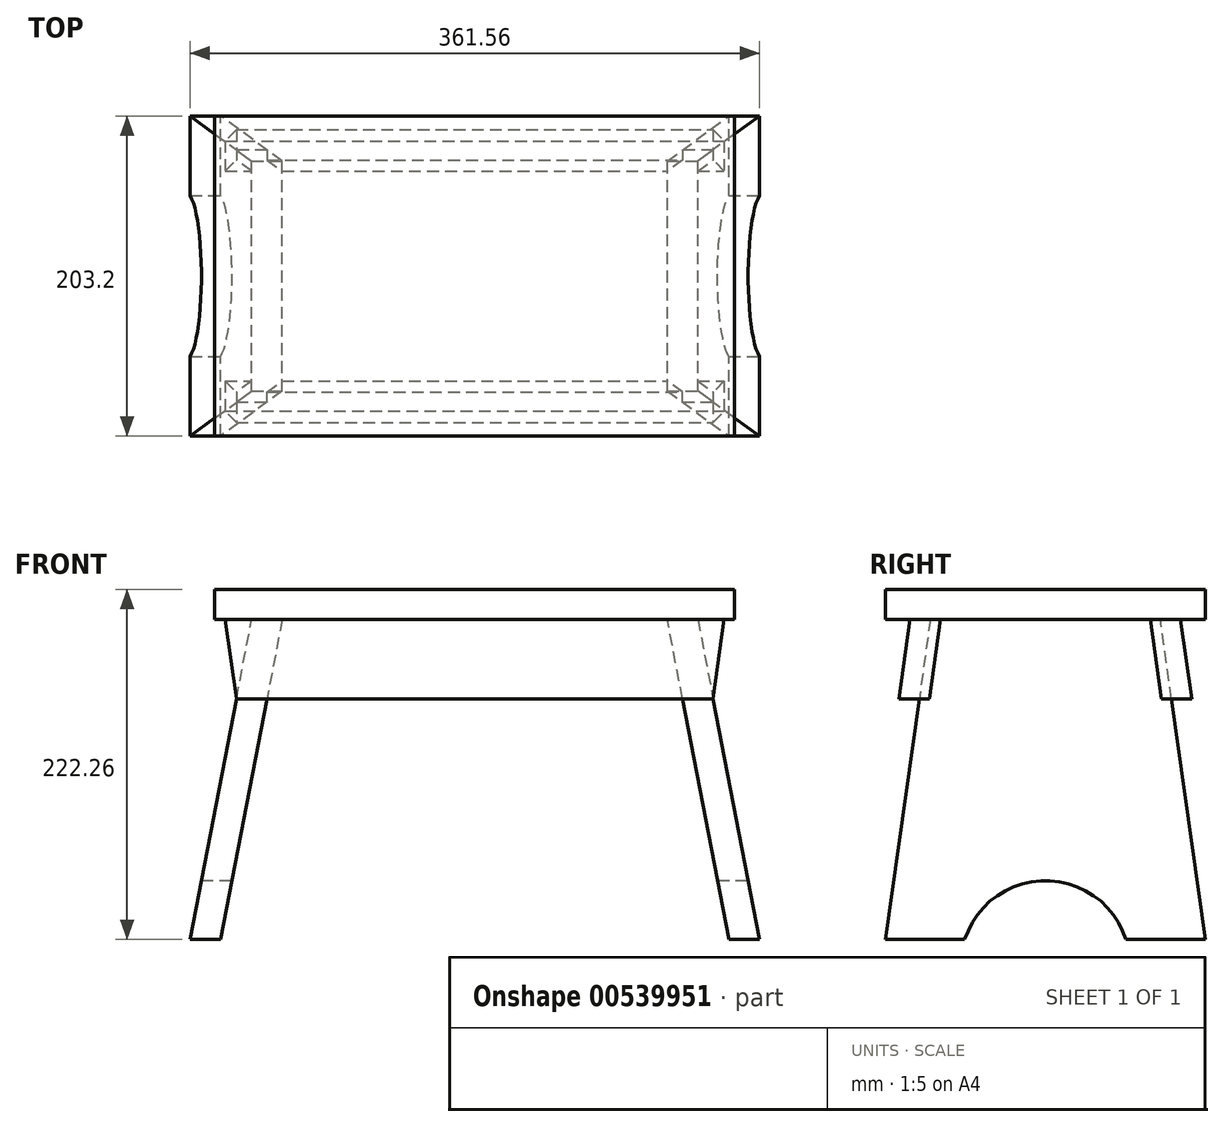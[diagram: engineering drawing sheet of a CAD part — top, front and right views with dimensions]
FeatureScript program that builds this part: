
annotation { "Feature Type Name" : "Feature", "Feature Type Description" : "" }
export const myFeature = defineFeature(function(context is Context, id is Id, definition is map)
    precondition{}
    {
        {
            var Q0;
            Q0=qCreatedBy(makeId("Front.planeOp"),FACE);
            var sketch = newSketch(context, id + "F0", { "sketchPlane" : qUnion([Q0])});
            skLineSegment(sketch, "E0.bottom", {"start": v(-165.1, 9.52) * mm, "end": v(165.1, 9.53) * mm});
            skLineSegment(sketch, "E0.top", {"start": v(-165.1, -9.53) * mm, "end": v(165.1, -9.52) * mm});
            skLineSegment(sketch, "E0.left", {"start": v(-165.1, 9.52) * mm, "end": v(-165.1, -9.53) * mm});
            skLineSegment(sketch, "E0.right", {"start": v(165.1, 9.52) * mm, "end": v(165.1, -9.53) * mm});
            skPoint(sketch, "E0.middle", {"position": v(0, 0) * mm});
            skLineSegment(sketch, "E1.bottom", {"start": v(-165.1, -9.53) * mm, "end": v(165.1, -9.52) * mm, "construction": true});
            skLineSegment(sketch, "E2", {"start": v(141.68, -9.53) * mm, "end": v(180.78, -212.73) * mm});
            skLineSegment(sketch, "E3", {"start": v(180.78, -212.73) * mm, "end": v(161.38, -212.73) * mm});
            skLineSegment(sketch, "E4", {"start": v(161.38, -212.73) * mm, "end": v(122.28, -9.52) * mm});
            skLineSegment(sketch, "E5", {"start": v(0, 0) * mm, "end": v(0, -212.72) * mm, "construction": true});
            skLineSegment(sketch, "E6.MirrorCS", {"start": v(-180.78, -212.73) * mm, "end": v(-161.38, -212.73) * mm});
            skLineSegment(sketch, "E7.MirrorCS", {"start": v(165.1, -9.52) * mm, "end": v(-165.1, -9.52) * mm});
            skLineSegment(sketch, "E8.MirrorCS", {"start": v(165.1, -9.53) * mm, "end": v(-165.1, -9.53) * mm, "construction": true});
            skLineSegment(sketch, "E9.MirrorCS", {"start": v(-141.68, -9.53) * mm, "end": v(-180.78, -212.73) * mm});
            skLineSegment(sketch, "E10.MirrorCS", {"start": v(-161.38, -212.73) * mm, "end": v(-122.28, -9.53) * mm});
            skLineSegment(sketch, "E11.bottom", {"start": v(-165.1, -9.53) * mm, "end": v(165.1, -9.53) * mm});
            skLineSegment(sketch, "E11.top", {"start": v(-165.1, -59.83) * mm, "end": v(165.1, -59.83) * mm});
            skLineSegment(sketch, "E11.left", {"start": v(-165.1, -9.53) * mm, "end": v(-165.1, -59.83) * mm});
            skLineSegment(sketch, "E11.right", {"start": v(165.1, -9.53) * mm, "end": v(165.1, -59.83) * mm});
            skLineSegment(sketch, "E12", {"start": v(151.36, -59.83) * mm, "end": v(158.43, -9.53) * mm});
            skLineSegment(sketch, "E13.MirrorCS", {"start": v(-151.36, -59.83) * mm, "end": v(-158.43, -9.53) * mm});
            skLineSegment(sketch, "E14.bottom", {"start": v(-165.1, -9.53) * mm, "end": v(165.1, -9.53) * mm, "construction": true});
            skLineSegment(sketch, "E14.top", {"start": v(-165.1, -212.73) * mm, "end": v(165.1, -212.73) * mm, "construction": true});
            skLineSegment(sketch, "E14.left", {"start": v(-165.1, -9.53) * mm, "end": v(-165.1, -212.73) * mm, "construction": true});
            skLineSegment(sketch, "E14.right", {"start": v(165.1, -9.53) * mm, "end": v(165.1, -212.73) * mm, "construction": true});
            skSolve(sketch);
        }
        {
            var Q0;
            {var subQ0=sQuery(id+"F0.wireOp",EDGE,"E0.right");Q0=makeQuery(id+"F0.imprint","IMPRINT",FACE,{"disambiguationData":[TD([[makeQuery(id+"F0.imprint","IMPRINT",EDGE,{"derivedFrom":subQ0}),-1.0]])]});}
            extrude(context, id + "F1", {"entities" : qUnion([Q0]), "endBound" : BoundingType.SYMMETRIC, "oppositeDirection" : true, "depth" : 203.2 * mm, "offsetDistance" : 25.4 * mm});
        }
        {
            var Q0;
            {var subQ0=sQuery(id+"F0.wireOp",EDGE,"E6.MirrorCS");Q0=makeQuery(id+"F0.imprint","IMPRINT",FACE,{"disambiguationData":[TD([[makeQuery(id+"F0.imprint","IMPRINT",EDGE,{"derivedFrom":subQ0}),1.0]])]});}
            var Q1;
            {var subQ0=sQuery(id+"F0.wireOp",EDGE,"E3");Q1=makeQuery(id+"F0.imprint","IMPRINT",FACE,{"disambiguationData":[TD([[makeQuery(id+"F0.imprint","IMPRINT",EDGE,{"derivedFrom":subQ0}),-1.0]])]});}
            var Q2;
            {var subQ0=sQuery(id+"F0.wireOp",EDGE,"E11.top");var subQ1=sQuery(id+"F0.wireOp",EDGE,"E2");var subQ2=makeQuery(id+"F0.imprint","INTERSECT",VERTEX,{"derivedFrom":[subQ1,subQ0]});Q2=makeQuery(id+"F0.imprint","IMPRINT",FACE,{"disambiguationData":[TD([[makeQuery(id+"F0.imprint","IMPRINT",EDGE,{"disambiguationData":[TD([[subQ2,1.0]])],"derivedFrom":subQ1}),-1.0]])]});}
            var Q3;
            {var subQ0=sQuery(id+"F0.wireOp",EDGE,"E9.MirrorCS");var subQ1=sQuery(id+"F0.wireOp",EDGE,"E0.top");var subQ2=makeQuery(id+"F0.imprint","INTERSECT",VERTEX,{"derivedFrom":[subQ1,subQ0]});Q3=makeQuery(id+"F0.imprint","IMPRINT",FACE,{"disambiguationData":[TD([[makeQuery(id+"F0.imprint","IMPRINT",EDGE,{"disambiguationData":[TD([[subQ2,-1.0]])],"derivedFrom":subQ1}),-1.0]])]});}
            var Q4;
            {var subQ0=sQuery(id+"F0.wireOp",EDGE,"E11.bottom");var subQ5=sQuery(id+"F0.wireOp",EDGE,"E10.MirrorCS");var subQ6=makeQuery(id+"F0.imprint","INTERSECT",VERTEX,{"derivedFrom":[subQ5,subQ0]});Q4=makeQuery(id+"F0.imprint","IMPRINT",FACE,{"disambiguationData":[TD([[makeQuery(id+"F0.imprint","IMPRINT",EDGE,{"disambiguationData":[TD([[subQ6,1.0]])],"derivedFrom":subQ5}),1.0]])]});}
            var Q5;
            Q5=makeQuery(id+"F1.opExtrude","CAP_VERTEX",VERTEX,{"disambiguationData":[OSD([sQuery(id+"F0.wireOp",EDGE,"E0.left"),sQuery(id+"F0.wireOp",EDGE,"E11.bottom")])],"isStart":true});
            var Q6;
            Q6=makeQuery(id+"F1.opExtrude","CAP_VERTEX",VERTEX,{"disambiguationData":[OSD([sQuery(id+"F0.wireOp",EDGE,"E0.left"),sQuery(id+"F0.wireOp",EDGE,"E11.bottom")])],"isStart":false});
            extrude(context, id + "F2", {"entities" : qUnion([Q0, Q1, Q2, Q3, Q4]), "endBound" : BoundingType.UP_TO_VERTEX, "depth" : 25.4 * mm, "endBoundEntityVertex" : qUnion([Q5]), "offsetDistance" : 25.4 * mm, "hasSecondDirection" : true, "secondDirectionBound" : SecondDirectionBoundingType.UP_TO_VERTEX, "secondDirectionOppositeDirection" : true, "secondDirectionDepth" : 25.4 * mm, "secondDirectionBoundEntityVertex" : qUnion([Q6])});
        }
        {
            var Q0;
            Q0=qCreatedBy(makeId("Right.planeOp"),FACE);
            var sketch = newSketch(context, id + "F3", { "sketchPlane" : qUnion([Q0])});
            skLineSegment(sketch, "E15.0.0", {"start": v(101.6, -9.52) * mm, "end": v(-101.6, -9.52) * mm});
            skLineSegment(sketch, "E15.0.1", {"start": v(-101.6, -9.52) * mm, "end": v(-101.6, -212.72) * mm});
            skLineSegment(sketch, "E15.0.2", {"start": v(-101.6, -212.73) * mm, "end": v(101.6, -212.73) * mm});
            skLineSegment(sketch, "E15.0.3", {"start": v(101.6, -212.72) * mm, "end": v(101.6, -9.52) * mm});
            skLineSegment(sketch, "E16", {"start": v(-101.6, -212.72) * mm, "end": v(-73.04, -9.52) * mm});
            skLineSegment(sketch, "E17.MirrorCS", {"start": v(101.6, -9.52) * mm, "end": v(101.6, -212.72) * mm});
            skLineSegment(sketch, "E18.MirrorCS", {"start": v(101.6, -212.72) * mm, "end": v(73.04, -9.52) * mm});
            skArc(sketch, "E19", {"start": v(51.24, -212.72) * mm, "mid": v(0, -175.24) * mm, "end": v(-51.24, -212.72) * mm});
            skLineSegment(sketch, "E20", {"start": v(0, -229) * mm, "end": v(0, -212.72) * mm, "construction": true});
            skLineSegment(sketch, "E21.0.0", {"start": v(101.6, -9.53) * mm, "end": v(-101.6, -9.53) * mm});
            skLineSegment(sketch, "E22.0.1", {"start": v(-101.6, -9.53) * mm, "end": v(101.6, -9.53) * mm});
            skSolve(sketch);
        }
        {
            var Q0;
            {var subQ0=sQuery(id+"F3.wireOp",EDGE,"E16");Q0=makeQuery(id+"F3.imprint","IMPRINT",FACE,{"disambiguationData":[TD([[makeQuery(id+"F3.imprint","IMPRINT",EDGE,{"derivedFrom":subQ0}),1.0]])]});}
            var Q1;
            {var subQ0=sQuery(id+"F3.wireOp",EDGE,"E19");Q1=makeQuery(id+"F3.imprint","IMPRINT",FACE,{"disambiguationData":[TD([[makeQuery(id+"F3.imprint","IMPRINT",EDGE,{"derivedFrom":subQ0}),1.0]])]});}
            var Q2;
            {var subQ0=sQuery(id+"F3.wireOp",EDGE,"E18.MirrorCS");Q2=makeQuery(id+"F3.imprint","IMPRINT",FACE,{"disambiguationData":[TD([[makeQuery(id+"F3.imprint","IMPRINT",EDGE,{"derivedFrom":subQ0}),-1.0]])]});}
            extrude(context, id + "F4", {"entities" : qUnion([Q0, Q1, Q2]), "operationType" : NewBodyOperationType.REMOVE, "endBound" : BoundingType.THROUGH_ALL, "oppositeDirection" : true, "depth" : 25.4 * mm, "offsetDistance" : 25.4 * mm, "hasSecondDirection" : true, "secondDirectionBound" : SecondDirectionBoundingType.THROUGH_ALL, "secondDirectionOppositeDirection" : false, "secondDirectionDepth" : 25.4 * mm});
        }
        {
            var Q0;
            Q0=qCreatedBy(makeId("Right.planeOp"),FACE);
            var sketch = newSketch(context, id + "F5", { "sketchPlane" : qUnion([Q0])});
            skLineSegment(sketch, "E23.0", {"start": v(-73.04, -9.52) * mm, "end": v(-101.6, -212.73) * mm});
            skLineSegment(sketch, "E24.0", {"start": v(101.68, -9.52) * mm, "end": v(-101.6, -9.52) * mm});
            skLineSegment(sketch, "E25", {"start": v(-73.04, -9.52) * mm, "end": v(-85.87, -9.52) * mm});
            skLineSegment(sketch, "E26", {"start": v(-85.87, -9.53) * mm, "end": v(-92.94, -59.83) * mm});
            skLineSegment(sketch, "E27", {"start": v(-92.94, -59.83) * mm, "end": v(-73.7, -59.83) * mm});
            skLineSegment(sketch, "E28", {"start": v(-73.7, -59.83) * mm, "end": v(-66.63, -9.53) * mm});
            skLineSegment(sketch, "E29", {"start": v(-66.63, -9.52) * mm, "end": v(-85.87, -9.52) * mm});
            skLineSegment(sketch, "E30", {"start": v(-73.7, -59.83) * mm, "end": v(0, -59.83) * mm, "construction": true});
            skLineSegment(sketch, "E31.MirrorCS", {"start": v(-80.11, -59.83) * mm, "end": v(-101.44, -211.62) * mm});
            skLineSegment(sketch, "E32.MirrorCS", {"start": v(73.04, -9.52) * mm, "end": v(85.87, -9.52) * mm});
            skLineSegment(sketch, "E33.MirrorCS", {"start": v(73.7, -59.83) * mm, "end": v(66.63, -9.53) * mm});
            skLineSegment(sketch, "E34.MirrorCS", {"start": v(92.94, -59.83) * mm, "end": v(73.7, -59.83) * mm});
            skLineSegment(sketch, "E35.MirrorCS", {"start": v(66.63, -9.52) * mm, "end": v(85.87, -9.52) * mm});
            skLineSegment(sketch, "E36.MirrorCS", {"start": v(85.87, -9.53) * mm, "end": v(92.94, -59.83) * mm});
            skLineSegment(sketch, "E37.0", {"start": v(73.04, -9.52) * mm, "end": v(101.6, -212.72) * mm});
            skSolve(sketch);
        }
        {
            var Q0;
            {var subQ5=sQuery(id+"F5.wireOp",EDGE,"E26");Q0=makeQuery(id+"F5.imprint","IMPRINT",FACE,{"disambiguationData":[TD([[makeQuery(id+"F5.imprint","IMPRINT",EDGE,{"derivedFrom":subQ5}),1.0]])]});}
            var Q1;
            {var subQ0=sQuery(id+"F5.wireOp",EDGE,"E33.MirrorCS");Q1=makeQuery(id+"F5.imprint","IMPRINT",FACE,{"disambiguationData":[TD([[makeQuery(id+"F5.imprint","IMPRINT",EDGE,{"derivedFrom":subQ0}),-1.0]])]});}
            var Q2;
            {var subQ5=sQuery(id+"F5.wireOp",EDGE,"E28");Q2=makeQuery(id+"F5.imprint","IMPRINT",FACE,{"disambiguationData":[TD([[makeQuery(id+"F5.imprint","IMPRINT",EDGE,{"derivedFrom":subQ5}),1.0]])]});}
            var Q3;
            {var subQ0=sQuery(id+"F5.wireOp",EDGE,"E36.MirrorCS");Q3=makeQuery(id+"F5.imprint","IMPRINT",FACE,{"disambiguationData":[TD([[makeQuery(id+"F5.imprint","IMPRINT",EDGE,{"derivedFrom":subQ0}),-1.0]])]});}
            var Q4;
            Q4=makeQuery(id+"F1.opExtrude","SWEPT_FACE",FACE,{"disambiguationData":[OSD([sQuery(id+"F0.wireOp",EDGE,"E0.left")])]});
            var Q5;
            Q5=makeQuery(id+"F1.opExtrude","SWEPT_FACE",FACE,{"disambiguationData":[OSD([sQuery(id+"F0.wireOp",EDGE,"E0.right")])]});
            extrude(context, id + "F6", {"entities" : qUnion([Q0, Q1, Q2, Q3]), "endBound" : BoundingType.UP_TO_SURFACE, "oppositeDirection" : true, "depth" : 25.4 * mm, "endBoundEntityFace" : qUnion([Q4]), "offsetDistance" : 25.4 * mm, "hasSecondDirection" : true, "secondDirectionBound" : SecondDirectionBoundingType.UP_TO_SURFACE, "secondDirectionOppositeDirection" : false, "secondDirectionDepth" : 25.4 * mm, "secondDirectionBoundEntityFace" : qUnion([Q5])});
        }
        {
            var Q0;
            {var subQ0=sQuery(id+"F0.wireOp",EDGE,"E11.left");Q0=makeQuery(id+"F0.imprint","IMPRINT",FACE,{"disambiguationData":[TD([[makeQuery(id+"F0.imprint","IMPRINT",EDGE,{"derivedFrom":subQ0}),1.0]])]});}
            var Q1;
            {var subQ0=sQuery(id+"F0.wireOp",EDGE,"E11.right");Q1=makeQuery(id+"F0.imprint","IMPRINT",FACE,{"disambiguationData":[TD([[makeQuery(id+"F0.imprint","IMPRINT",EDGE,{"derivedFrom":subQ0}),-1.0]])]});}
            extrude(context, id + "F7", {"entities" : qUnion([Q0, Q1]), "operationType" : NewBodyOperationType.REMOVE, "endBound" : BoundingType.THROUGH_ALL, "oppositeDirection" : true, "depth" : 25.4 * mm, "offsetDistance" : 25.4 * mm, "hasSecondDirection" : true, "secondDirectionBound" : SecondDirectionBoundingType.THROUGH_ALL, "secondDirectionOppositeDirection" : false, "secondDirectionDepth" : 25.4 * mm});
        }
        {
            var Q0;
            Q0=makeQuery(id+"F2.opExtrude","SWEPT_BODY",BODY,{"disambiguationData":[OSD([sQuery(id+"F0.wireOp",EDGE,"E6.MirrorCS"),sQuery(id+"F0.wireOp",EDGE,"E9.MirrorCS"),sQuery(id+"F0.wireOp",EDGE,"E10.MirrorCS"),sQuery(id+"F0.wireOp",EDGE,"E11.bottom")])]});
            var Q1;
            Q1=makeQuery(id+"F6.opExtrude","SWEPT_BODY",BODY,{"disambiguationData":[OSD([sQuery(id+"F5.wireOp",EDGE,"E33.MirrorCS"),sQuery(id+"F5.wireOp",EDGE,"E34.MirrorCS"),sQuery(id+"F5.wireOp",EDGE,"E35.MirrorCS"),sQuery(id+"F5.wireOp",EDGE,"E36.MirrorCS")])]});
            booleanBodies(context, id + "F8", {"operationType" : BooleanOperationType.SUBTRACTION, "tools" : qUnion([Q0]), "targets" : qUnion([Q1]), "keepTools" : true});
        }
        {
            var Q0;
            Q0=makeQuery(id+"F2.opExtrude","SWEPT_BODY",BODY,{"disambiguationData":[OSD([sQuery(id+"F0.wireOp",EDGE,"E6.MirrorCS"),sQuery(id+"F0.wireOp",EDGE,"E9.MirrorCS"),sQuery(id+"F0.wireOp",EDGE,"E10.MirrorCS"),sQuery(id+"F0.wireOp",EDGE,"E11.bottom")])]});
            var Q1;
            Q1=makeQuery(id+"F6.opExtrude","SWEPT_BODY",BODY,{"disambiguationData":[OSD([sQuery(id+"F5.wireOp",EDGE,"E26"),sQuery(id+"F5.wireOp",EDGE,"E27"),sQuery(id+"F5.wireOp",EDGE,"E28"),sQuery(id+"F5.wireOp",EDGE,"E29")])]});
            booleanBodies(context, id + "F9", {"operationType" : BooleanOperationType.SUBTRACTION, "tools" : qUnion([Q0]), "targets" : qUnion([Q1]), "keepTools" : true});
        }
        {
            var Q0;
            Q0=makeQuery(id+"F2.opExtrude","SWEPT_BODY",BODY,{"disambiguationData":[OSD([sQuery(id+"F0.wireOp",EDGE,"E2"),sQuery(id+"F0.wireOp",EDGE,"E3"),sQuery(id+"F0.wireOp",EDGE,"E4"),sQuery(id+"F0.wireOp",EDGE,"E11.bottom")])]});
            var Q1;
            Q1=makeQuery(id+"F6.opExtrude","SWEPT_BODY",BODY,{"disambiguationData":[OSD([sQuery(id+"F5.wireOp",EDGE,"E26"),sQuery(id+"F5.wireOp",EDGE,"E27"),sQuery(id+"F5.wireOp",EDGE,"E28"),sQuery(id+"F5.wireOp",EDGE,"E29")])]});
            booleanBodies(context, id + "F10", {"operationType" : BooleanOperationType.SUBTRACTION, "tools" : qUnion([Q0]), "targets" : qUnion([Q1]), "keepTools" : true});
        }
        {
            var Q0;
            Q0=makeQuery(id+"F2.opExtrude","SWEPT_BODY",BODY,{"disambiguationData":[OSD([sQuery(id+"F0.wireOp",EDGE,"E2"),sQuery(id+"F0.wireOp",EDGE,"E3"),sQuery(id+"F0.wireOp",EDGE,"E4"),sQuery(id+"F0.wireOp",EDGE,"E11.bottom")])]});
            var Q1;
            Q1=makeQuery(id+"F6.opExtrude","SWEPT_BODY",BODY,{"disambiguationData":[OSD([sQuery(id+"F5.wireOp",EDGE,"E33.MirrorCS"),sQuery(id+"F5.wireOp",EDGE,"E34.MirrorCS"),sQuery(id+"F5.wireOp",EDGE,"E35.MirrorCS"),sQuery(id+"F5.wireOp",EDGE,"E36.MirrorCS")])]});
            booleanBodies(context, id + "F11", {"operationType" : BooleanOperationType.SUBTRACTION, "tools" : qUnion([Q0]), "targets" : qUnion([Q1]), "keepTools" : true});
        }
    });
